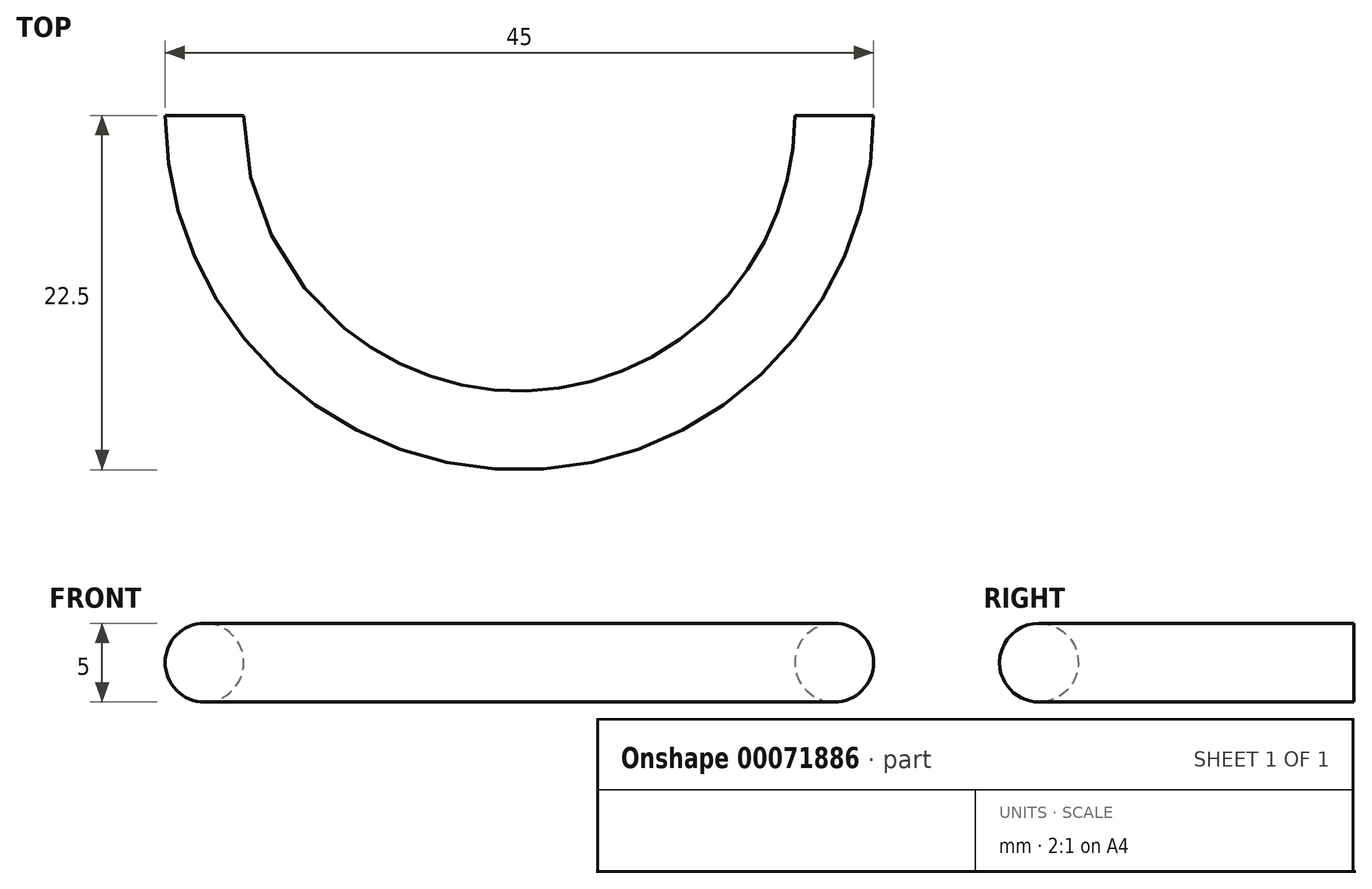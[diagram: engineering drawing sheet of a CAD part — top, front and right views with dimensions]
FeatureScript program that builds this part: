
annotation { "Feature Type Name" : "Feature", "Feature Type Description" : "" }
export const myFeature = defineFeature(function(context is Context, id is Id, definition is map)
    precondition{}
    {
        {
            var Q0;
            Q0=qCreatedBy(makeId("Top.planeOp"),FACE);
            var sketch = newSketch(context, id + "F0", { "sketchPlane" : qUnion([Q0])});
            skArc(sketch, "E0", {"start": v(-20, 0) * mm, "mid": v(0, -20) * mm, "end": v(20, 0) * mm});
            skSolve(sketch);
        }
        {
            var Q0;
            Q0=qCreatedBy(makeId("Right.planeOp"),FACE);
            var sketch = newSketch(context, id + "F1", { "sketchPlane" : qUnion([Q0])});
            skCircle(sketch, "E1", {"center": v(-20, 0) * mm, "radius": 2.5 * mm});
            skSolve(sketch);
        }
        {
            var Q0;
            Q0=qSketchRegion(id+"F1",true);
            var Q1;
            Q1=qConstructionFilter(qBodyType(qCreatedBy(id+"F0",EDGE),BodyType.WIRE),ConstructionObject.NO);
            sweep(context, id + "F2", {"profiles" : qUnion([Q0]), "path" : qUnion([Q1])});
        }
    });
